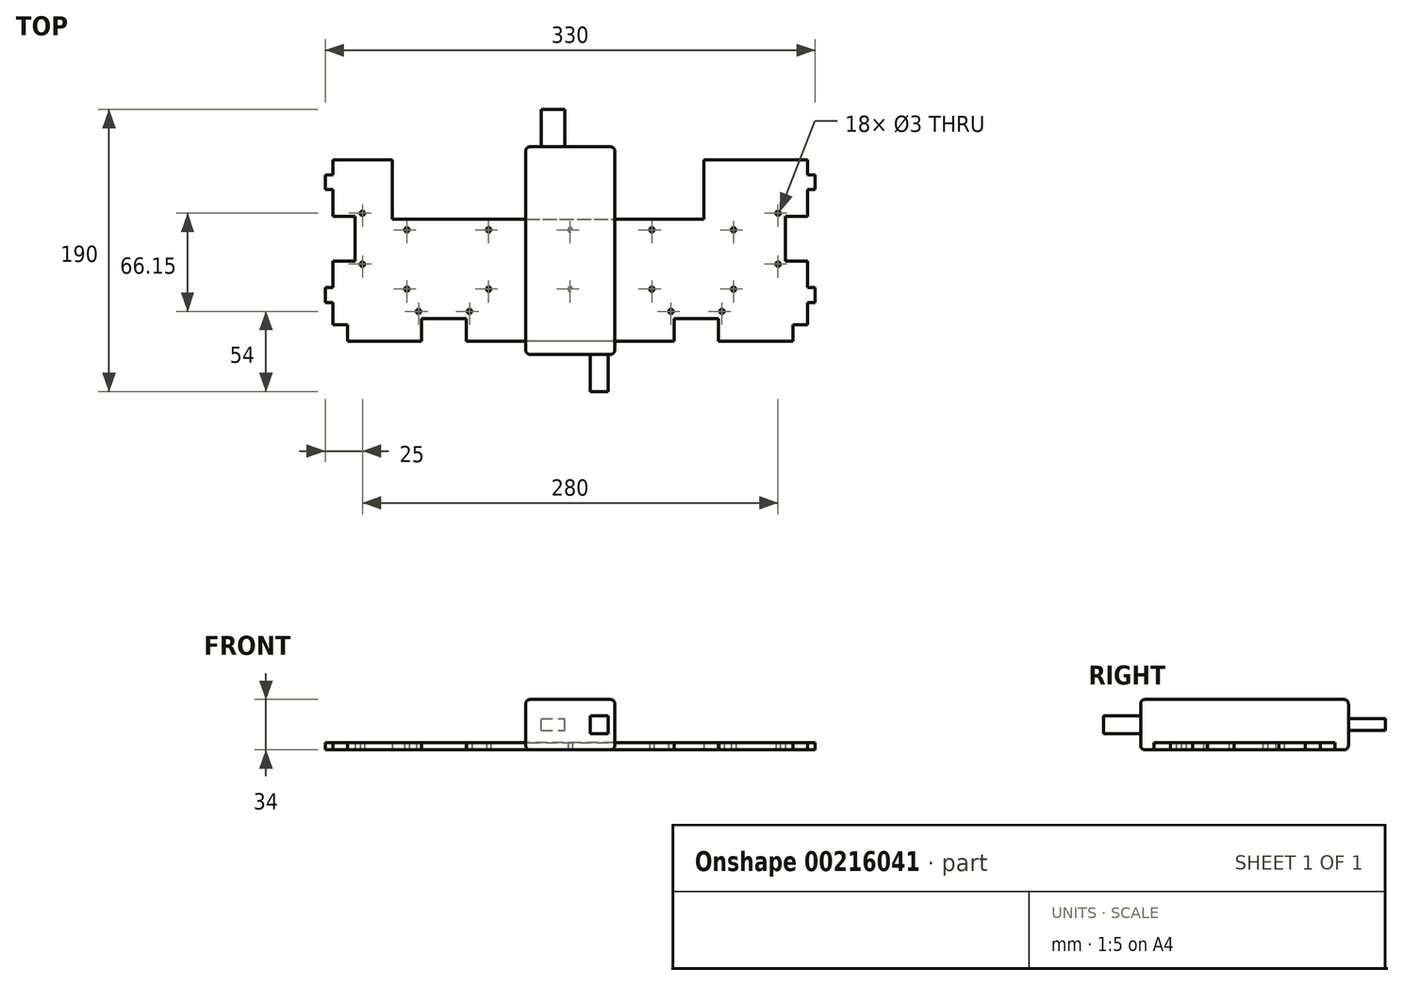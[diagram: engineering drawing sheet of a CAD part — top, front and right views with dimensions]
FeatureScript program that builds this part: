
annotation { "Feature Type Name" : "Feature", "Feature Type Description" : "" }
export const myFeature = defineFeature(function(context is Context, id is Id, definition is map)
    precondition{}
    {
        {
            var Q0;
            Q0=qCreatedBy(makeId("Top.planeOp"),FACE);
            var sketch = newSketch(context, id + "F0", { "sketchPlane" : qUnion([Q0])});
            skLineSegment(sketch, "E0.bottom", {"start": v(30, -70) * mm, "end": v(-30, -70) * mm});
            skLineSegment(sketch, "E0.top", {"start": v(30, 70) * mm, "end": v(-30, 70) * mm});
            skLineSegment(sketch, "E0.left", {"start": v(30, -70) * mm, "end": v(30, 70) * mm});
            skLineSegment(sketch, "E0.right", {"start": v(-30, -70) * mm, "end": v(-30, 70) * mm});
            skPoint(sketch, "E0.middle", {"position": v(0, 0) * mm});
            skSolve(sketch);
        }
        {
            var Q0;
            Q0 = qSketchRegion(id + "F0", true);
            extrude(context, id + "F1", {"entities" : qUnion([Q0]), "depth" : 34 * mm});
        }
        {
            var Q0;
            Q0=makeQuery(id+"F1.opExtrude","CAP_EDGE",EDGE,{"disambiguationData":[OSD([sQuery(id+"F0.wireOp",EDGE,"E0.bottom")])],"isStart":false});
            var Q1;
            Q1=makeQuery(id+"F1.opExtrude","CAP_EDGE",EDGE,{"disambiguationData":[OSD([sQuery(id+"F0.wireOp",EDGE,"E0.right")])],"isStart":false});
            var Q2;
            Q2=makeQuery(id+"F1.opExtrude","CAP_EDGE",EDGE,{"disambiguationData":[OSD([sQuery(id+"F0.wireOp",EDGE,"E0.top")])],"isStart":false});
            var Q3;
            Q3=makeQuery(id+"F1.opExtrude","CAP_EDGE",EDGE,{"disambiguationData":[OSD([sQuery(id+"F0.wireOp",EDGE,"E0.left")])],"isStart":false});
            var Q4;
            Q4=makeQuery(id+"F1.opExtrude","SWEPT_EDGE",EDGE,{"disambiguationData":[OSD([sQuery(id+"F0.wireOp",EDGE,"E0.bottom"),sQuery(id+"F0.wireOp",EDGE,"E0.left")])]});
            var Q5;
            Q5=makeQuery(id+"F1.opExtrude","SWEPT_EDGE",EDGE,{"disambiguationData":[OSD([sQuery(id+"F0.wireOp",EDGE,"E0.bottom"),sQuery(id+"F0.wireOp",EDGE,"E0.right")])]});
            var Q6;
            Q6=makeQuery(id+"F1.opExtrude","CAP_EDGE",EDGE,{"disambiguationData":[OSD([sQuery(id+"F0.wireOp",EDGE,"E0.bottom")])],"isStart":true});
            var Q7;
            Q7=makeQuery(id+"F1.opExtrude","CAP_EDGE",EDGE,{"disambiguationData":[OSD([sQuery(id+"F0.wireOp",EDGE,"E0.left")])],"isStart":true});
            var Q8;
            Q8=makeQuery(id+"F1.opExtrude","SWEPT_EDGE",EDGE,{"disambiguationData":[OSD([sQuery(id+"F0.wireOp",EDGE,"E0.top"),sQuery(id+"F0.wireOp",EDGE,"E0.left")])]});
            var Q9;
            Q9=makeQuery(id+"F1.opExtrude","CAP_EDGE",EDGE,{"disambiguationData":[OSD([sQuery(id+"F0.wireOp",EDGE,"E0.top")])],"isStart":true});
            var Q10;
            Q10=makeQuery(id+"F1.opExtrude","SWEPT_EDGE",EDGE,{"disambiguationData":[OSD([sQuery(id+"F0.wireOp",EDGE,"E0.top"),sQuery(id+"F0.wireOp",EDGE,"E0.right")])]});
            var Q11;
            Q11=makeQuery(id+"F1.opExtrude","CAP_EDGE",EDGE,{"disambiguationData":[OSD([sQuery(id+"F0.wireOp",EDGE,"E0.right")])],"isStart":true});
            fillet(context, id + "F2", {"entities" : qUnion([Q0, Q1, Q2, Q3, Q4, Q5, Q6, Q7, Q8, Q9, Q10, Q11]), "radius" : 3 * mm, "tangentPropagation" : true, "allowEdgeOverflow" : false});
        }
        {
            var Q0;
            Q0=makeQuery(id+"F1.opExtrude","SWEPT_FACE",FACE,{"disambiguationData":[OSD([sQuery(id+"F0.wireOp",EDGE,"E0.bottom")])]});
            var sketch = newSketch(context, id + "F3", { "sketchPlane" : qUnion([Q0])});
            skLineSegment(sketch, "E1.bottom", {"start": v(25.5, 11) * mm, "end": v(13.5, 11) * mm});
            skLineSegment(sketch, "E1.top", {"start": v(25.5, 23) * mm, "end": v(13.5, 23) * mm});
            skLineSegment(sketch, "E1.left", {"start": v(25.5, 11) * mm, "end": v(25.5, 23) * mm});
            skLineSegment(sketch, "E1.right", {"start": v(13.5, 11) * mm, "end": v(13.5, 23) * mm});
            skPoint(sketch, "E1.middle", {"position": v(19.5, 17) * mm});
            skPoint(sketch, "E1.middle.positionSnap0", {"position": v(27, 17) * mm});
            skPoint(sketch, "E1.centerSnap0", {"position": v(27, 17) * mm});
            skSolve(sketch);
        }
        {
            var Q0;
            Q0 = qSketchRegion(id + "F3", true);
            extrude(context, id + "F4", {"entities" : qUnion([Q0]), "operationType" : NewBodyOperationType.ADD, "depth" : 25 * mm});
        }
        {
            var Q0;
            Q0=makeQuery(id+"F1.opExtrude","SWEPT_FACE",FACE,{"disambiguationData":[OSD([sQuery(id+"F0.wireOp",EDGE,"E0.top")])]});
            var sketch = newSketch(context, id + "F5", { "sketchPlane" : qUnion([Q0])});
            skLineSegment(sketch, "E2.bottom", {"start": v(19.5, 13) * mm, "end": v(3.5, 13) * mm});
            skLineSegment(sketch, "E2.top", {"start": v(19.5, 21) * mm, "end": v(3.5, 21) * mm});
            skLineSegment(sketch, "E2.left", {"start": v(19.5, 13) * mm, "end": v(19.5, 21) * mm});
            skLineSegment(sketch, "E2.right", {"start": v(3.5, 13) * mm, "end": v(3.5, 21) * mm});
            skPoint(sketch, "E2.middle", {"position": v(11.5, 17) * mm});
            skPoint(sketch, "E2.middle.positionSnap0", {"position": v(27, 17) * mm});
            skPoint(sketch, "E2.centerSnap0", {"position": v(27, 17) * mm});
            skSolve(sketch);
        }
        {
            var Q0;
            Q0 = qSketchRegion(id + "F5", true);
            extrude(context, id + "F6", {"entities" : qUnion([Q0]), "operationType" : NewBodyOperationType.ADD, "depth" : 25 * mm});
        }
        {
            var Q0;
            Q0=qCreatedBy(makeId("Top.planeOp"),FACE);
            var sketch = newSketch(context, id + "F7", { "sketchPlane" : qUnion([Q0])});
            skLineSegment(sketch, "E3.bottom", {"start": v(160, -61) * mm, "end": v(-160, -61) * mm});
            skLineSegment(sketch, "E3.top", {"start": v(160, 61) * mm, "end": v(-160, 61) * mm});
            skLineSegment(sketch, "E3.left", {"start": v(160, -61) * mm, "end": v(160, 61) * mm});
            skLineSegment(sketch, "E3.right", {"start": v(-160, -61) * mm, "end": v(-160, 61) * mm});
            skPoint(sketch, "E3.middle", {"position": v(0, 0) * mm});
            skLineSegment(sketch, "E4.bottom", {"start": v(-160, 51) * mm, "end": v(-165, 51) * mm});
            skLineSegment(sketch, "E4.top", {"start": v(-160, 41) * mm, "end": v(-165, 41) * mm});
            skLineSegment(sketch, "E4.left", {"start": v(-160, 51) * mm, "end": v(-160, 41) * mm});
            skLineSegment(sketch, "E4.right", {"start": v(-165, 51) * mm, "end": v(-165, 41) * mm});
            skLineSegment(sketch, "E5.bottom", {"start": v(-160, -25) * mm, "end": v(-165, -25) * mm});
            skLineSegment(sketch, "E5.top", {"start": v(-160, -35) * mm, "end": v(-165, -35) * mm});
            skLineSegment(sketch, "E5.left", {"start": v(-160, -25) * mm, "end": v(-160, -35) * mm});
            skLineSegment(sketch, "E5.right", {"start": v(-165, -25) * mm, "end": v(-165, -35) * mm});
            skLineSegment(sketch, "E6.bottom", {"start": v(160, 41) * mm, "end": v(165, 41) * mm});
            skLineSegment(sketch, "E6.top", {"start": v(160, 51) * mm, "end": v(165, 51) * mm});
            skLineSegment(sketch, "E6.left", {"start": v(160, 51) * mm, "end": v(160, 41) * mm});
            skLineSegment(sketch, "E6.right", {"start": v(165, 51) * mm, "end": v(165, 41) * mm});
            skLineSegment(sketch, "E7.bottom", {"start": v(160, -25) * mm, "end": v(165, -25) * mm});
            skLineSegment(sketch, "E7.top", {"start": v(160, -35) * mm, "end": v(165, -35) * mm});
            skLineSegment(sketch, "E7.left", {"start": v(160, -25) * mm, "end": v(160, -35) * mm});
            skLineSegment(sketch, "E7.right", {"start": v(165, -25) * mm, "end": v(165, -35) * mm});
            skLineSegment(sketch, "E8", {"start": v(-104.5, 0) * mm, "end": v(104.74, 0) * mm, "construction": true});
            skCircle(sketch, "E9", {"center": v(-140, -9.15) * mm, "radius": 1.5 * mm});
            skCircle(sketch, "E10", {"center": v(-140, 25.15) * mm, "radius": 1.5 * mm});
            skCircle(sketch, "E11", {"center": v(-102.15, -41) * mm, "radius": 1.5 * mm});
            skCircle(sketch, "E12", {"center": v(-67.85, -41) * mm, "radius": 1.5 * mm});
            skCircle(sketch, "E13", {"center": v(67.85, -41) * mm, "radius": 1.5 * mm});
            skCircle(sketch, "E14", {"center": v(102.15, -41) * mm, "radius": 1.5 * mm});
            skCircle(sketch, "E15", {"center": v(140, 25.15) * mm, "radius": 1.5 * mm});
            skCircle(sketch, "E16", {"center": v(140, -9.15) * mm, "radius": 1.5 * mm});
            skLineSegment(sketch, "E17.bottom", {"start": v(-160, 23) * mm, "end": v(-145, 23) * mm});
            skLineSegment(sketch, "E17.top", {"start": v(-160, -7) * mm, "end": v(-145, -7) * mm});
            skLineSegment(sketch, "E17.left", {"start": v(-160, 23) * mm, "end": v(-160, -7) * mm});
            skLineSegment(sketch, "E17.right", {"start": v(-145, 23) * mm, "end": v(-145, -7) * mm});
            skLineSegment(sketch, "E18.bottom", {"start": v(160, 23) * mm, "end": v(145, 23) * mm});
            skLineSegment(sketch, "E18.top", {"start": v(160, -7) * mm, "end": v(145, -7) * mm});
            skLineSegment(sketch, "E18.left", {"start": v(160, 23) * mm, "end": v(160, -7) * mm});
            skLineSegment(sketch, "E18.right", {"start": v(145, 23) * mm, "end": v(145, -7) * mm});
            skLineSegment(sketch, "E19.bottom", {"start": v(-100, -61) * mm, "end": v(-70, -61) * mm});
            skLineSegment(sketch, "E19.top", {"start": v(-100, -46) * mm, "end": v(-70, -46) * mm});
            skLineSegment(sketch, "E19.left", {"start": v(-100, -61) * mm, "end": v(-100, -46) * mm});
            skLineSegment(sketch, "E19.right", {"start": v(-70, -61) * mm, "end": v(-70, -46) * mm});
            skLineSegment(sketch, "E20.bottom", {"start": v(70, -61) * mm, "end": v(100, -61) * mm});
            skLineSegment(sketch, "E20.top", {"start": v(70, -46) * mm, "end": v(100, -46) * mm});
            skLineSegment(sketch, "E20.left", {"start": v(70, -61) * mm, "end": v(70, -46) * mm});
            skLineSegment(sketch, "E20.right", {"start": v(100, -61) * mm, "end": v(100, -46) * mm});
            skLineSegment(sketch, "E21", {"start": v(-85, -55.84) * mm, "end": v(-85, -36.9) * mm, "construction": true});
            skPoint(sketch, "E21.startSnap0", {"position": v(-85, -46) * mm});
            skLineSegment(sketch, "E22", {"start": v(85, -56.44) * mm, "end": v(85, -36.38) * mm, "construction": true});
            skPoint(sketch, "E22.startSnap0", {"position": v(85, -46) * mm});
            skLineSegment(sketch, "E23", {"start": v(-103.3, 8) * mm, "end": v(105.18, 8) * mm, "construction": true});
            skLineSegment(sketch, "E24.bottom", {"start": v(-160, -61) * mm, "end": v(-150, -61) * mm});
            skLineSegment(sketch, "E24.top", {"start": v(-160, -50) * mm, "end": v(-150, -50) * mm});
            skLineSegment(sketch, "E24.left", {"start": v(-160, -61) * mm, "end": v(-160, -50) * mm});
            skLineSegment(sketch, "E24.right", {"start": v(-150, -61) * mm, "end": v(-150, -50) * mm});
            skLineSegment(sketch, "E25.bottom", {"start": v(160, -61) * mm, "end": v(150, -61) * mm});
            skLineSegment(sketch, "E25.top", {"start": v(160, -50) * mm, "end": v(150, -50) * mm});
            skLineSegment(sketch, "E25.left", {"start": v(160, -61) * mm, "end": v(160, -50) * mm});
            skLineSegment(sketch, "E25.right", {"start": v(150, -61) * mm, "end": v(150, -50) * mm});
            skLineSegment(sketch, "E26.bottom", {"start": v(-120, 61) * mm, "end": v(90, 61) * mm});
            skLineSegment(sketch, "E26.top", {"start": v(-120, 21) * mm, "end": v(90, 21) * mm});
            skLineSegment(sketch, "E26.left", {"start": v(-120, 61) * mm, "end": v(-120, 21) * mm});
            skLineSegment(sketch, "E26.right", {"start": v(90, 61) * mm, "end": v(90, 21) * mm});
            skCircle(sketch, "E27", {"center": v(-110, -26) * mm, "radius": 1.5 * mm});
            skCircle(sketch, "E28.0.1.0", {"center": v(-110, 14) * mm, "radius": 1.5 * mm});
            skCircle(sketch, "E28.1.0.0", {"center": v(-55, -26) * mm, "radius": 1.5 * mm});
            skCircle(sketch, "E28.1.1.0", {"center": v(-55, 14) * mm, "radius": 1.5 * mm});
            skCircle(sketch, "E28.2.0.0", {"center": v(0, -26) * mm, "radius": 1.5 * mm});
            skCircle(sketch, "E28.2.1.0", {"center": v(0, 14) * mm, "radius": 1.5 * mm});
            skCircle(sketch, "E28.3.0.0", {"center": v(55, -26) * mm, "radius": 1.5 * mm});
            skCircle(sketch, "E28.3.1.0", {"center": v(55, 14) * mm, "radius": 1.5 * mm});
            skCircle(sketch, "E28.4.0.0", {"center": v(110, -26) * mm, "radius": 1.5 * mm});
            skCircle(sketch, "E28.4.1.0", {"center": v(110, 14) * mm, "radius": 1.5 * mm});
            skLineSegment(sketch, "E28.direction1", {"start": v(-110, -26) * mm, "end": v(-55, -26) * mm, "construction": true});
            skLineSegment(sketch, "E28.direction2", {"start": v(-110, -26) * mm, "end": v(-110, 14) * mm, "construction": true});
            skSolve(sketch);
        }
        {
            var Q0;
            Q0=makeQuery(id+"F7.imprint","IMPRINT",FACE,{"disambiguationData":[TD([[makeQuery(id+"F7.imprint","IMPRINT",EDGE,{"derivedFrom":sQuery(id+"F7.wireOp",EDGE,"E4.bottom")}),1.0]])]});
            var Q1;
            Q1=makeQuery(id+"F7.imprint","IMPRINT",FACE,{"disambiguationData":[TD([[makeQuery(id+"F7.imprint","IMPRINT",EDGE,{"derivedFrom":sQuery(id+"F7.wireOp",EDGE,"E5.bottom")}),1.0]])]});
            var Q2;
            Q2=makeQuery(id+"F7.imprint","IMPRINT",FACE,{"disambiguationData":[TD([[makeQuery(id+"F7.imprint","IMPRINT",EDGE,{"derivedFrom":sQuery(id+"F7.wireOp",EDGE,"E6.bottom")}),1.0]])]});
            var Q3;
            Q3=makeQuery(id+"F7.imprint","IMPRINT",FACE,{"disambiguationData":[TD([[makeQuery(id+"F7.imprint","IMPRINT",EDGE,{"derivedFrom":sQuery(id+"F7.wireOp",EDGE,"E7.bottom")}),-1.0]])]});
            var Q4;
            {var subQ7=sQuery(id+"F7.wireOp",EDGE,"E3.bottom");Q4=makeQuery(id+"F7.imprint","IMPRINT",FACE,{"disambiguationData":[TD([[makeQuery(id+"F7.imprint","IMPRINT",EDGE,{"derivedFrom":subQ7}),-1.0]])]});}
            extrude(context, id + "F8", {"entities" : qUnion([Q0, Q1, Q2, Q3, Q4]), "depth" : 5 * mm});
        }
    });
